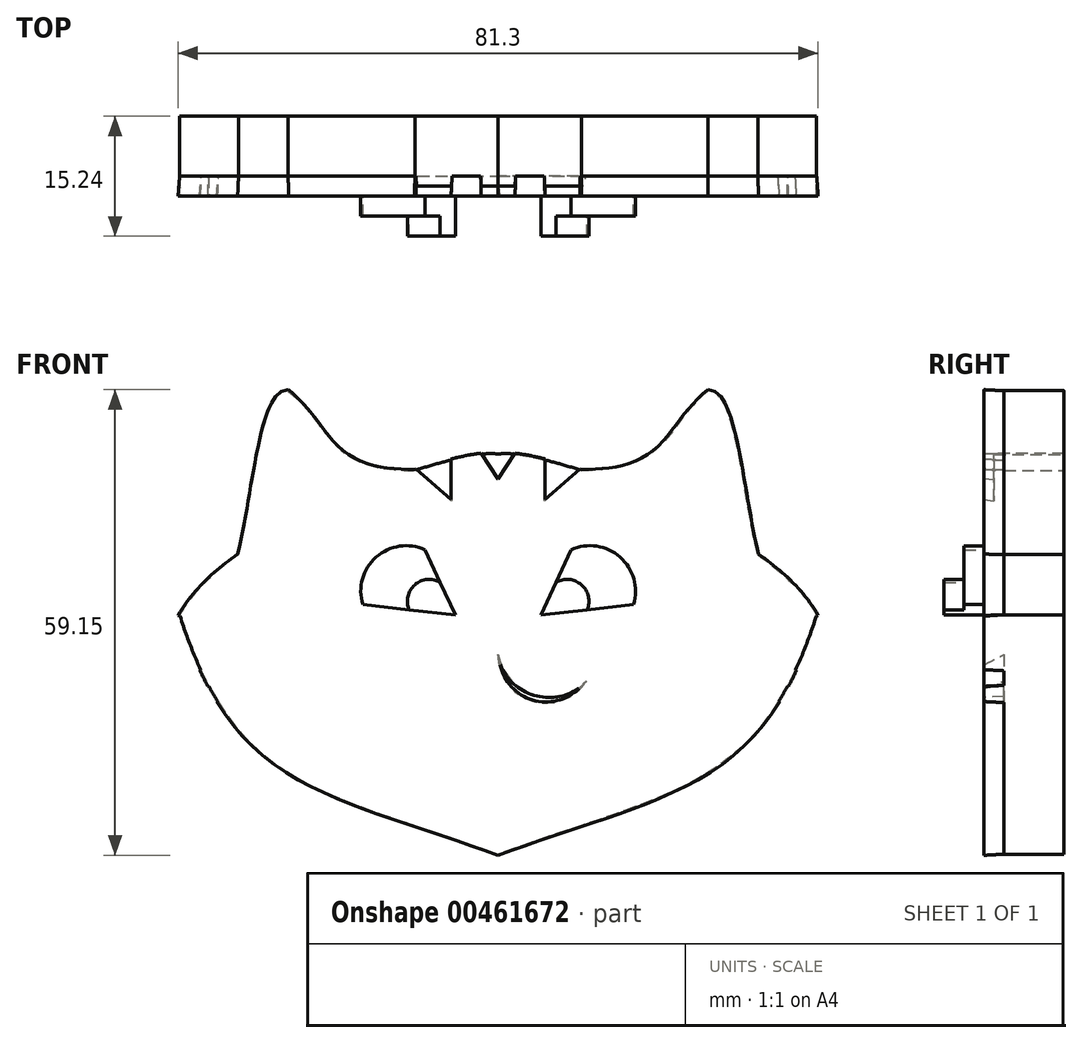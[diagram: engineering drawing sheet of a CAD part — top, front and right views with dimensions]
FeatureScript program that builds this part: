
annotation { "Feature Type Name" : "Feature", "Feature Type Description" : "" }
export const myFeature = defineFeature(function(context is Context, id is Id, definition is map)
    precondition{}
    {
        {
            var Q0;
            Q0=qCreatedBy(makeId("Front.planeOp"),FACE);
            var sketch = newSketch(context, id + "F0", { "sketchPlane" : qUnion([Q0])});
            skFitSpline(sketch, "E0", {"points": [v(0, 20.4) * mm, v(-40.46, 0) * mm], "startDerivative": vector(-12.86, 3.44) * mm, "endDerivative": vector(-19.39, -35.25) * mm});
            skFitSpline(sketch, "E1.MirrorCS", {"points": [v(0, 20.4) * mm, v(40.46, 0) * mm], "startDerivative": vector(12.86, 3.44) * mm, "endDerivative": vector(19.39, -35.25) * mm});
            skFitSpline(sketch, "E2", {"points": [v(-40.46, 0) * mm, v(0, -30.4) * mm], "startDerivative": vector(21.14, -66.24) * mm, "endDerivative": vector(67.82, -24.49) * mm});
            skFitSpline(sketch, "E3.MirrorCS", {"points": [v(40.46, 0) * mm, v(0, -30.4) * mm], "startDerivative": vector(-21.14, -66.24) * mm, "endDerivative": vector(-67.82, -24.49) * mm});
            skFitSpline(sketch, "E4", {"points": [v(-32.98, 7.64) * mm, v(-26.67, 28.46) * mm], "startDerivative": vector(5.7, 22.1) * mm, "endDerivative": vector(10.73, -0.98) * mm});
            skFitSpline(sketch, "E5.MirrorCS", {"points": [v(32.98, 7.64) * mm, v(26.67, 28.46) * mm], "startDerivative": vector(-5.7, 22.1) * mm, "endDerivative": vector(-10.73, -0.98) * mm});
            skFitSpline(sketch, "E6", {"points": [v(-26.67, 28.46) * mm, v(-10.58, 18.35) * mm], "startDerivative": vector(16.59, -13.17) * mm, "endDerivative": vector(33.64, 0.57) * mm});
            skFitSpline(sketch, "E7.MirrorCS", {"points": [v(26.67, 28.46) * mm, v(10.58, 18.35) * mm], "startDerivative": vector(-16.59, -13.17) * mm, "endDerivative": vector(-33.64, 0.57) * mm});
            skSolve(sketch);
        }
        {
            var Q0;
            Q0 = qSketchRegion(id + "F0", true);
            extrude(context, id + "F1", {"entities" : qUnion([Q0]), "depth" : 7.62 * mm});
        }
        {
            var Q0;
            Q0=makeQuery(id+"F1.opExtrude","CAP_FACE",FACE,{"disambiguationData":[OSD([sQuery(id+"F0.wireOp",EDGE,"E0"),sQuery(id+"F0.wireOp",EDGE,"E1.MirrorCS"),sQuery(id+"F0.wireOp",EDGE,"E2"),sQuery(id+"F0.wireOp",EDGE,"E3.MirrorCS"),sQuery(id+"F0.wireOp",EDGE,"E4"),sQuery(id+"F0.wireOp",EDGE,"E5.MirrorCS"),sQuery(id+"F0.wireOp",EDGE,"E6"),sQuery(id+"F0.wireOp",EDGE,"E7.MirrorCS")])],"isStart":false});
            var sketch = newSketch(context, id + "F2", { "sketchPlane" : qUnion([Q0])});
            skLineSegment(sketch, "E8", {"start": v(-5.44, 0) * mm, "end": v(-9.27, 8.25) * mm});
            skLineSegment(sketch, "E9", {"start": v(-5.44, 0) * mm, "end": v(-22.3, 1.85) * mm});
            skArc(sketch, "E10", {"start": v(-9.27, 8.25) * mm, "mid": v(-19.05, 11.7) * mm, "end": v(-22.3, 1.85) * mm});
            skLineSegment(sketch, "E11.MirrorCS", {"start": v(5.44, 0) * mm, "end": v(9.27, 8.25) * mm});
            skArc(sketch, "E12.MirrorCS", {"start": v(9.27, 8.25) * mm, "mid": v(19.05, 11.7) * mm, "end": v(22.3, 1.85) * mm});
            skLineSegment(sketch, "E13.MirrorCS", {"start": v(5.44, 0) * mm, "end": v(22.3, 1.85) * mm});
            skFitSpline(sketch, "E14", {"points": [v(-2.88, 0) * mm, v(2.72, 0) * mm, v(0, -4.15) * mm, v(-2.88, 0) * mm]});
            skSolve(sketch);
        }
        {
            var Q0;
            Q0 = qSketchRegion(id + "F2", true);
            extrude(context, id + "F3", {"entities" : qUnion([Q0]), "operationType" : NewBodyOperationType.ADD, "depth" : 2.54 * mm});
        }
        {
            var Q0;
            Q0=makeQuery(id+"F3.opExtrude","CAP_FACE",FACE,{"disambiguationData":[OSD([sQuery(id+"F2.wireOp",EDGE,"E8"),sQuery(id+"F2.wireOp",EDGE,"E9"),sQuery(id+"F2.wireOp",EDGE,"E10")])],"isStart":false});
            var sketch = newSketch(context, id + "F4", { "sketchPlane" : qUnion([Q0])});
            skArc(sketch, "E15", {"start": v(-9.27, 8.25) * mm, "mid": v(-15.49, 7.34) * mm, "end": v(-17.19, 1.3) * mm});
            skArc(sketch, "E16.MirrorCS", {"start": v(9.27, 8.25) * mm, "mid": v(15.49, 7.34) * mm, "end": v(17.19, 1.3) * mm});
            skLineSegment(sketch, "E17", {"start": v(-9.27, 8.25) * mm, "end": v(-5.44, 0) * mm});
            skLineSegment(sketch, "E18", {"start": v(-5.44, 0) * mm, "end": v(-17.19, 1.3) * mm});
            skLineSegment(sketch, "E19.MirrorCS", {"start": v(9.27, 8.25) * mm, "end": v(5.44, 0) * mm});
            skLineSegment(sketch, "E20.MirrorCS", {"start": v(5.44, 0) * mm, "end": v(17.19, 1.3) * mm});
            skSolve(sketch);
        }
        {
            var Q0;
            Q0 = qSketchRegion(id + "F4", true);
            extrude(context, id + "F5", {"entities" : qUnion([Q0]), "operationType" : NewBodyOperationType.ADD, "depth" : 2.54 * mm});
        }
        {
            var Q0;
            Q0=makeQuery(id+"F5.opExtrude","CAP_FACE",FACE,{"disambiguationData":[OSD([sQuery(id+"F4.wireOp",EDGE,"E15"),sQuery(id+"F4.wireOp",EDGE,"E17"),sQuery(id+"F4.wireOp",EDGE,"E18")])],"isStart":false});
            var sketch = newSketch(context, id + "F6", { "sketchPlane" : qUnion([Q0])});
            skArc(sketch, "E21", {"start": v(-7.35, 4.12) * mm, "mid": v(-10.59, 3.81) * mm, "end": v(-11.31, 0.65) * mm});
            skPoint(sketch, "E21.midSnap0", {"position": v(-11.31, 0.65) * mm});
            skPoint(sketch, "E21.midSnap1", {"position": v(-7.35, 4.12) * mm});
            skArc(sketch, "E22.MirrorCS", {"start": v(7.35, 4.12) * mm, "mid": v(10.59, 3.81) * mm, "end": v(11.31, 0.65) * mm});
            skLineSegment(sketch, "E23", {"start": v(-7.35, 4.12) * mm, "end": v(-5.44, 0) * mm});
            skLineSegment(sketch, "E24", {"start": v(-5.44, 0) * mm, "end": v(-11.31, 0.65) * mm});
            skLineSegment(sketch, "E25.MirrorCS", {"start": v(7.35, 4.12) * mm, "end": v(5.44, 0) * mm});
            skLineSegment(sketch, "E26.MirrorCS", {"start": v(5.44, 0) * mm, "end": v(11.31, 0.65) * mm});
            skSolve(sketch);
        }
        {
            var Q0;
            Q0 = qSketchRegion(id + "F6", true);
            extrude(context, id + "F7", {"entities" : qUnion([Q0]), "operationType" : NewBodyOperationType.ADD, "depth" : 2.54 * mm});
        }
        {
            var Q0;
            Q0=makeQuery(id+"F1.opExtrude","CAP_FACE",FACE,{"disambiguationData":[OSD([sQuery(id+"F0.wireOp",EDGE,"E0"),sQuery(id+"F0.wireOp",EDGE,"E1.MirrorCS"),sQuery(id+"F0.wireOp",EDGE,"E2"),sQuery(id+"F0.wireOp",EDGE,"E3.MirrorCS"),sQuery(id+"F0.wireOp",EDGE,"E4"),sQuery(id+"F0.wireOp",EDGE,"E5.MirrorCS"),sQuery(id+"F0.wireOp",EDGE,"E6"),sQuery(id+"F0.wireOp",EDGE,"E7.MirrorCS")])],"isStart":false});
            var sketch = newSketch(context, id + "F8", { "sketchPlane" : qUnion([Q0])});
            skLineSegment(sketch, "E27", {"start": v(-40.46, 0) * mm, "end": v(-21.36, -7.1) * mm});
            skLineSegment(sketch, "E28", {"start": v(-21.36, -7.1) * mm, "end": v(-37.73, -7.1) * mm});
            skLineSegment(sketch, "E29", {"start": v(-36.8, -8.96) * mm, "end": v(-26.62, -11.15) * mm});
            skLineSegment(sketch, "E30", {"start": v(-26.62, -11.15) * mm, "end": v(-35.54, -11.15) * mm});
            skLineSegment(sketch, "E31.MirrorCS", {"start": v(40.46, 0) * mm, "end": v(21.36, -7.1) * mm});
            skLineSegment(sketch, "E32.MirrorCS", {"start": v(21.36, -7.1) * mm, "end": v(37.73, -7.1) * mm});
            skLineSegment(sketch, "E33.MirrorCS", {"start": v(36.8, -8.96) * mm, "end": v(26.62, -11.15) * mm});
            skLineSegment(sketch, "E34.MirrorCS", {"start": v(26.62, -11.15) * mm, "end": v(35.54, -11.15) * mm});
            skLineSegment(sketch, "E35", {"start": v(-10.44, 18.4) * mm, "end": v(-5.85, 14.33) * mm});
            skLineSegment(sketch, "E36", {"start": v(-5.85, 14.33) * mm, "end": v(-5.85, 19.7) * mm});
            skLineSegment(sketch, "E37", {"start": v(-2.22, 20.4) * mm, "end": v(0, 17.03) * mm});
            skLineSegment(sketch, "E38.MirrorCS", {"start": v(2.22, 20.4) * mm, "end": v(0, 17.03) * mm});
            skLineSegment(sketch, "E39.MirrorCS", {"start": v(5.85, 14.33) * mm, "end": v(5.85, 19.7) * mm});
            skLineSegment(sketch, "E40.MirrorCS", {"start": v(10.44, 18.4) * mm, "end": v(5.85, 14.33) * mm});
            skSolve(sketch);
        }
        {
            var Q0;
            {var subQ0=sQuery(id+"F8.wireOp",EDGE,"E27");Q0=makeQuery(id+"F8.imprint","IMPRINT",FACE,{"disambiguationData":[TD([[makeQuery(id+"F8.imprint","IMPRINT",EDGE,{"derivedFrom":subQ0}),-1.0]])]});}
            var Q1;
            {var subQ0=sQuery(id+"F8.wireOp",EDGE,"E29");Q1=makeQuery(id+"F8.imprint","IMPRINT",FACE,{"disambiguationData":[TD([[makeQuery(id+"F8.imprint","IMPRINT",EDGE,{"derivedFrom":subQ0}),-1.0]])]});}
            var Q2;
            {var subQ0=sQuery(id+"F8.wireOp",EDGE,"E31.MirrorCS");Q2=makeQuery(id+"F8.imprint","IMPRINT",FACE,{"disambiguationData":[TD([[makeQuery(id+"F8.imprint","IMPRINT",EDGE,{"derivedFrom":subQ0}),1.0]])]});}
            var Q3;
            {var subQ0=sQuery(id+"F8.wireOp",EDGE,"E34.MirrorCS");Q3=makeQuery(id+"F8.imprint","IMPRINT",FACE,{"disambiguationData":[TD([[makeQuery(id+"F8.imprint","IMPRINT",EDGE,{"derivedFrom":subQ0}),1.0]])]});}
            extrude(context, id + "F9", {"entities" : qUnion([Q0, Q1, Q2, Q3]), "operationType" : NewBodyOperationType.ADD, "depth" : 2.54 * mm});
        }
        {
            var Q0;
            {var subQ0=sQuery(id+"F8.wireOp",EDGE,"E35");Q0=makeQuery(id+"F8.imprint","IMPRINT",FACE,{"disambiguationData":[TD([[makeQuery(id+"F8.imprint","IMPRINT",EDGE,{"derivedFrom":subQ0}),1.0]])]});}
            var Q1;
            {var subQ0=sQuery(id+"F8.wireOp",EDGE,"E37");Q1=makeQuery(id+"F8.imprint","IMPRINT",FACE,{"disambiguationData":[TD([[makeQuery(id+"F8.imprint","IMPRINT",EDGE,{"derivedFrom":subQ0}),1.0]])]});}
            var Q2;
            {var subQ0=sQuery(id+"F8.wireOp",EDGE,"E39.MirrorCS");Q2=makeQuery(id+"F8.imprint","IMPRINT",FACE,{"disambiguationData":[TD([[makeQuery(id+"F8.imprint","IMPRINT",EDGE,{"derivedFrom":subQ0}),-1.0]])]});}
            extrude(context, id + "F10", {"entities" : qUnion([Q0, Q1, Q2]), "operationType" : NewBodyOperationType.ADD, "depth" : 1.27 * mm});
        }
        {
            var Q0;
            Q0=makeQuery(id+"F1.opExtrude","CAP_FACE",FACE,{"disambiguationData":[OSD([sQuery(id+"F0.wireOp",EDGE,"E0"),sQuery(id+"F0.wireOp",EDGE,"E1.MirrorCS"),sQuery(id+"F0.wireOp",EDGE,"E2"),sQuery(id+"F0.wireOp",EDGE,"E3.MirrorCS"),sQuery(id+"F0.wireOp",EDGE,"E4"),sQuery(id+"F0.wireOp",EDGE,"E5.MirrorCS"),sQuery(id+"F0.wireOp",EDGE,"E6"),sQuery(id+"F0.wireOp",EDGE,"E7.MirrorCS")])],"isStart":false});
            var sketch = newSketch(context, id + "F11", { "sketchPlane" : qUnion([Q0])});
            skCircle(sketch, "E41", {"center": v(43.28, 30.93) * mm, "radius": 6.17 * mm});
            skSolve(sketch);
        }
        {
            var Q0;
            Q0=makeQuery(id+"F11.imprint","IMPRINT",FACE,{"disambiguationData":[TD([[makeQuery(id+"F11.imprint","IMPRINT",EDGE,{"derivedFrom":sQuery(id+"F11.wireOp",EDGE,"E41")}),1.0]])]});
            extrude(context, id + "F12", {"entities" : qUnion([Q0]), "operationType" : NewBodyOperationType.REMOVE, "oppositeDirection" : true, "depth" : 25.4 * mm, "hasSecondDirection" : true, "secondDirectionOppositeDirection" : false, "secondDirectionDepth" : 41 * mm});
        }
        {
            var Q0;
            Q0=makeQuery(id+"F1.opExtrude","CAP_FACE",FACE,{"disambiguationData":[OSD([sQuery(id+"F0.wireOp",EDGE,"E0"),sQuery(id+"F0.wireOp",EDGE,"E1.MirrorCS"),sQuery(id+"F0.wireOp",EDGE,"E2"),sQuery(id+"F0.wireOp",EDGE,"E3.MirrorCS"),sQuery(id+"F0.wireOp",EDGE,"E4"),sQuery(id+"F0.wireOp",EDGE,"E5.MirrorCS"),sQuery(id+"F0.wireOp",EDGE,"E6"),sQuery(id+"F0.wireOp",EDGE,"E7.MirrorCS")])],"isStart":false});
            var sketch = newSketch(context, id + "F13", { "sketchPlane" : qUnion([Q0])});
            skArc(sketch, "E42", {"start": v(-11.2, -8.4) * mm, "mid": v(-4.33, -10.94) * mm, "end": v(0, -5.04) * mm});
            skArc(sketch, "E43", {"start": v(-11.2, -8.4) * mm, "mid": v(-4.59, -10.1) * mm, "end": v(0, -5.04) * mm});
            skArc(sketch, "E44.MirrorCS", {"start": v(11.2, -8.4) * mm, "mid": v(4.59, -10.1) * mm, "end": v(0, -5.04) * mm});
            skArc(sketch, "E45.MirrorCS", {"start": v(11.2, -8.4) * mm, "mid": v(4.33, -10.94) * mm, "end": v(0, -5.04) * mm});
            skFitSpline(sketch, "E46", {"points": [v(-3.21, -10.48) * mm, v(0, -16.1) * mm], "startDerivative": vector(-1.35, -10.4) * mm, "endDerivative": vector(5.35, -1.67) * mm});
            skFitSpline(sketch, "E47.MirrorCS", {"points": [v(3.21, -10.48) * mm, v(0, -16.1) * mm], "startDerivative": vector(1.35, -10.4) * mm, "endDerivative": vector(-5.35, -1.67) * mm});
            skSolve(sketch);
        }
        {
            var Q0;
            {var subQ0=sQuery(id+"F13.wireOp",EDGE,"E46");Q0=makeQuery(id+"F13.imprint","IMPRINT",FACE,{"disambiguationData":[TD([[makeQuery(id+"F13.imprint","IMPRINT",EDGE,{"derivedFrom":subQ0}),1.0]])]});}
            var Q1;
            {var subQ1=sQuery(id+"F13.wireOp",EDGE,"E44.MirrorCS");Q1=makeQuery(id+"F13.imprint","IMPRINT",FACE,{"disambiguationData":[TD([[makeQuery(id+"F13.imprint","IMPRINT",EDGE,{"derivedFrom":subQ1}),1.0]])]});}
            var Q2;
            {var subQ0=sQuery(id+"F13.wireOp",EDGE,"E43");Q2=makeQuery(id+"F13.imprint","IMPRINT",FACE,{"disambiguationData":[TD([[makeQuery(id+"F13.imprint","IMPRINT",EDGE,{"derivedFrom":subQ0}),-1.0]])]});}
            extrude(context, id + "F14", {"entities" : qUnion([Q0, Q1, Q2]), "operationType" : NewBodyOperationType.ADD, "depth" : 2.54 * mm, "hasDraft" : true, "draftAngle" : 3 * degree});
        }
        {
            var Q0;
            {var subQ0=sQuery(id+"F13.wireOp",EDGE,"E46");Q0=makeQuery(id+"F13.imprint","IMPRINT",FACE,{"disambiguationData":[TD([[makeQuery(id+"F13.imprint","IMPRINT",EDGE,{"derivedFrom":subQ0}),1.0]])]});}
            extrude(context, id + "F15", {"entities" : qUnion([Q0]), "operationType" : NewBodyOperationType.ADD, "depth" : 2.54 * mm});
        }
        {
            var Q0;
            {var subQ1=sQuery(id+"F13.wireOp",EDGE,"E44.MirrorCS");Q0=makeQuery(id+"F13.imprint","IMPRINT",FACE,{"disambiguationData":[TD([[makeQuery(id+"F13.imprint","IMPRINT",EDGE,{"derivedFrom":subQ1}),1.0]])]});}
            extrude(context, id + "F16", {"entities" : qUnion([Q0]), "operationType" : NewBodyOperationType.ADD, "depth" : 2.54 * mm});
        }
        {
            var Q0;
            {var subQ0=sQuery(id+"F13.wireOp",EDGE,"E43");Q0=makeQuery(id+"F13.imprint","IMPRINT",FACE,{"disambiguationData":[TD([[makeQuery(id+"F13.imprint","IMPRINT",EDGE,{"derivedFrom":subQ0}),-1.0]])]});}
            extrude(context, id + "F17", {"entities" : qUnion([Q0]), "operationType" : NewBodyOperationType.ADD, "depth" : 2.54 * mm});
        }
    });
